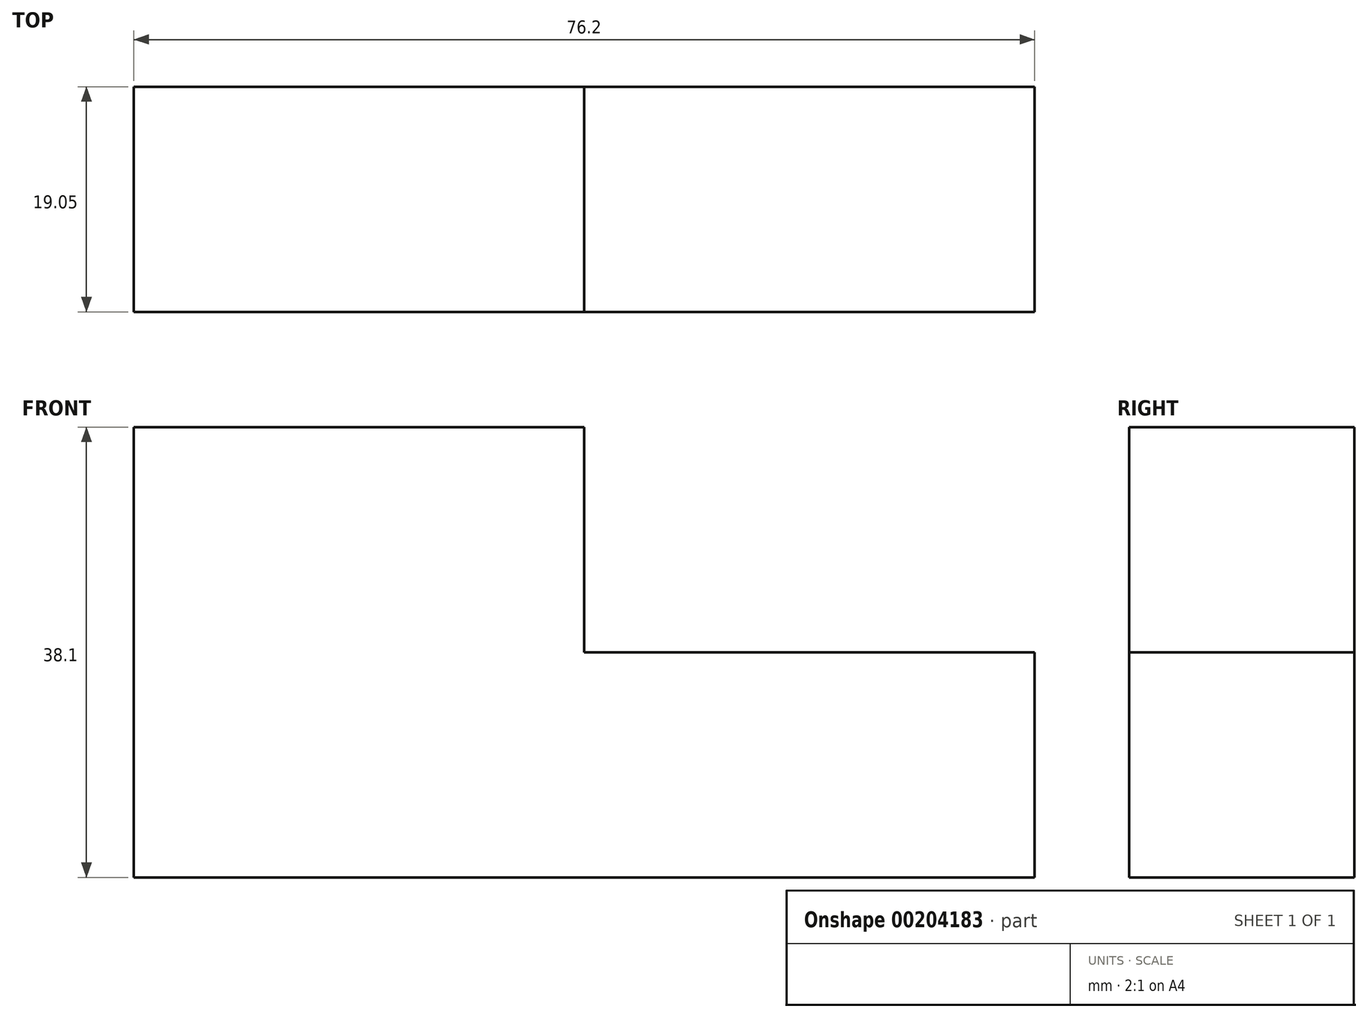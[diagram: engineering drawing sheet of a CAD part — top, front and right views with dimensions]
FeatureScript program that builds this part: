
annotation { "Feature Type Name" : "Feature", "Feature Type Description" : "" }
export const myFeature = defineFeature(function(context is Context, id is Id, definition is map)
    precondition{}
    {
        {
            var Q0;
            Q0=qCreatedBy(makeId("Front.planeOp"),FACE);
            var sketch = newSketch(context, id + "F0", { "sketchPlane" : qUnion([Q0])});
            skLineSegment(sketch, "E0.bottom", {"start": v(38.1, -19.05) * mm, "end": v(-38.1, -19.05) * mm});
            skLineSegment(sketch, "E0.top", {"start": v(0, 19.05) * mm, "end": v(-38.1, 19.05) * mm});
            skLineSegment(sketch, "E0.left", {"start": v(38.1, -19.05) * mm, "end": v(38.1, 0) * mm});
            skLineSegment(sketch, "E0.right", {"start": v(-38.1, -19.05) * mm, "end": v(-38.1, 19.05) * mm});
            skPoint(sketch, "E0.middle", {"position": v(0, 0) * mm});
            skLineSegment(sketch, "E1", {"start": v(38.1, 0) * mm, "end": v(0, 0) * mm});
            skPoint(sketch, "E2.start.orphan", {"position": v(0, 19.05) * mm});
            skPoint(sketch, "E3.orphan", {"position": v(38.1, 19.05) * mm});
            skLineSegment(sketch, "E4", {"start": v(0, 19.05) * mm, "end": v(0, 0) * mm});
            skSolve(sketch);
        }
        {
            var Q0;
            Q0=makeQuery(id+"F0.imprint","IMPRINT",FACE,{"disambiguationData":[TD([[makeQuery(id+"F0.imprint","IMPRINT",EDGE,{"derivedFrom":sQuery(id+"F0.wireOp",EDGE,"E0.bottom")}),-1.0]])]});
            extrude(context, id + "F1", {"entities" : qUnion([Q0]), "depth" : 19.05 * mm});
        }
    });
